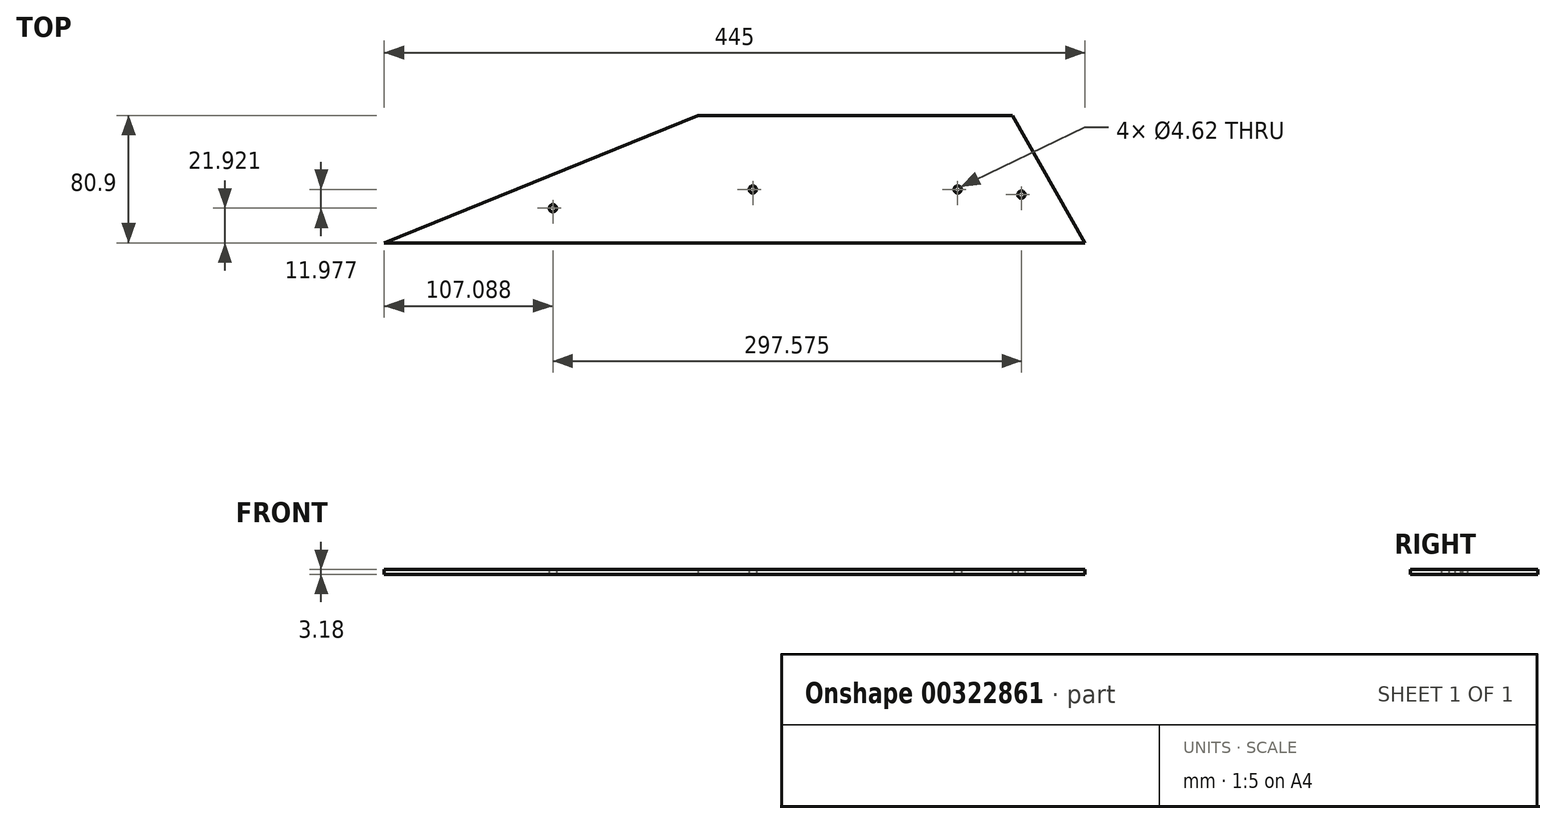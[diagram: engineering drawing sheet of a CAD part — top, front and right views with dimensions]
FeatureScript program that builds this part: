
annotation { "Feature Type Name" : "Feature", "Feature Type Description" : "" }
export const myFeature = defineFeature(function(context is Context, id is Id, definition is map)
    precondition{}
    {
        {
            var Q0;
            Q0=qCreatedBy(makeId("Top.planeOp"),FACE);
            var sketch = newSketch(context, id + "F0", { "sketchPlane" : qUnion([Q0])});
            skLineSegment(sketch, "E0.bottom", {"start": v(222.5, -40.45) * mm, "end": v(-222.5, -40.45) * mm});
            skLineSegment(sketch, "E0.top", {"start": v(176.62, 40.45) * mm, "end": v(-23.38, 40.45) * mm});
            skPoint(sketch, "E0.middle", {"position": v(0, 0) * mm});
            skLineSegment(sketch, "E1", {"start": v(176.62, 40.45) * mm, "end": v(222.5, -40.45) * mm});
            skPoint(sketch, "E2.end.orphan", {"position": v(222.5, 52.55) * mm});
            skPoint(sketch, "E0.left.end.orphan", {"position": v(222.5, 40.45) * mm});
            skLineSegment(sketch, "E3", {"start": v(-23.38, 40.45) * mm, "end": v(-222.5, -40.45) * mm});
            skLineSegment(sketch, "E4", {"start": v(-23.38, 40.45) * mm, "end": v(11.54, 40.45) * mm});
            skLineSegment(sketch, "E5", {"start": v(11.54, -4.24) * mm, "end": v(11.54, -6.55) * mm});
            skLineSegment(sketch, "E6", {"start": v(11.54, -6.55) * mm, "end": v(11.54, -4.24) * mm});
            skLineSegment(sketch, "E7", {"start": v(176.62, 40.45) * mm, "end": v(141.7, 40.45) * mm});
            skLineSegment(sketch, "E8", {"start": v(141.7, -4.24) * mm, "end": v(141.7, -6.55) * mm});
            skCircle(sketch, "E9", {"center": v(11.54, -6.55) * mm, "radius": 2.31 * mm});
            skCircle(sketch, "E10", {"center": v(141.7, -6.55) * mm, "radius": 2.31 * mm});
            skLineSegment(sketch, "E11", {"start": v(-116.28, -16.39) * mm, "end": v(-115.41, -18.53) * mm});
            skCircle(sketch, "E12", {"center": v(-115.41, -18.53) * mm, "radius": 2.31 * mm});
            skLineSegment(sketch, "E13", {"start": v(184.17, -8.73) * mm, "end": v(182.16, -9.87) * mm});
            skCircle(sketch, "E14", {"center": v(182.16, -9.87) * mm, "radius": 2.31 * mm});
            skPoint(sketch, "E0.right.end.orphan", {"position": v(-222.5, 40.45) * mm});
            skPoint(sketch, "E15.orphan", {"position": v(199.56, 0) * mm});
            skPoint(sketch, "E16.orphan", {"position": v(-122.94, 0) * mm});
            skSolve(sketch);
        }
        {
            var Q0;
            Q0 = qSketchRegion(id + "F0", true);
            extrude(context, id + "F1", {"entities" : qUnion([Q0]), "depth" : 3.17 * mm});
        }
    });
